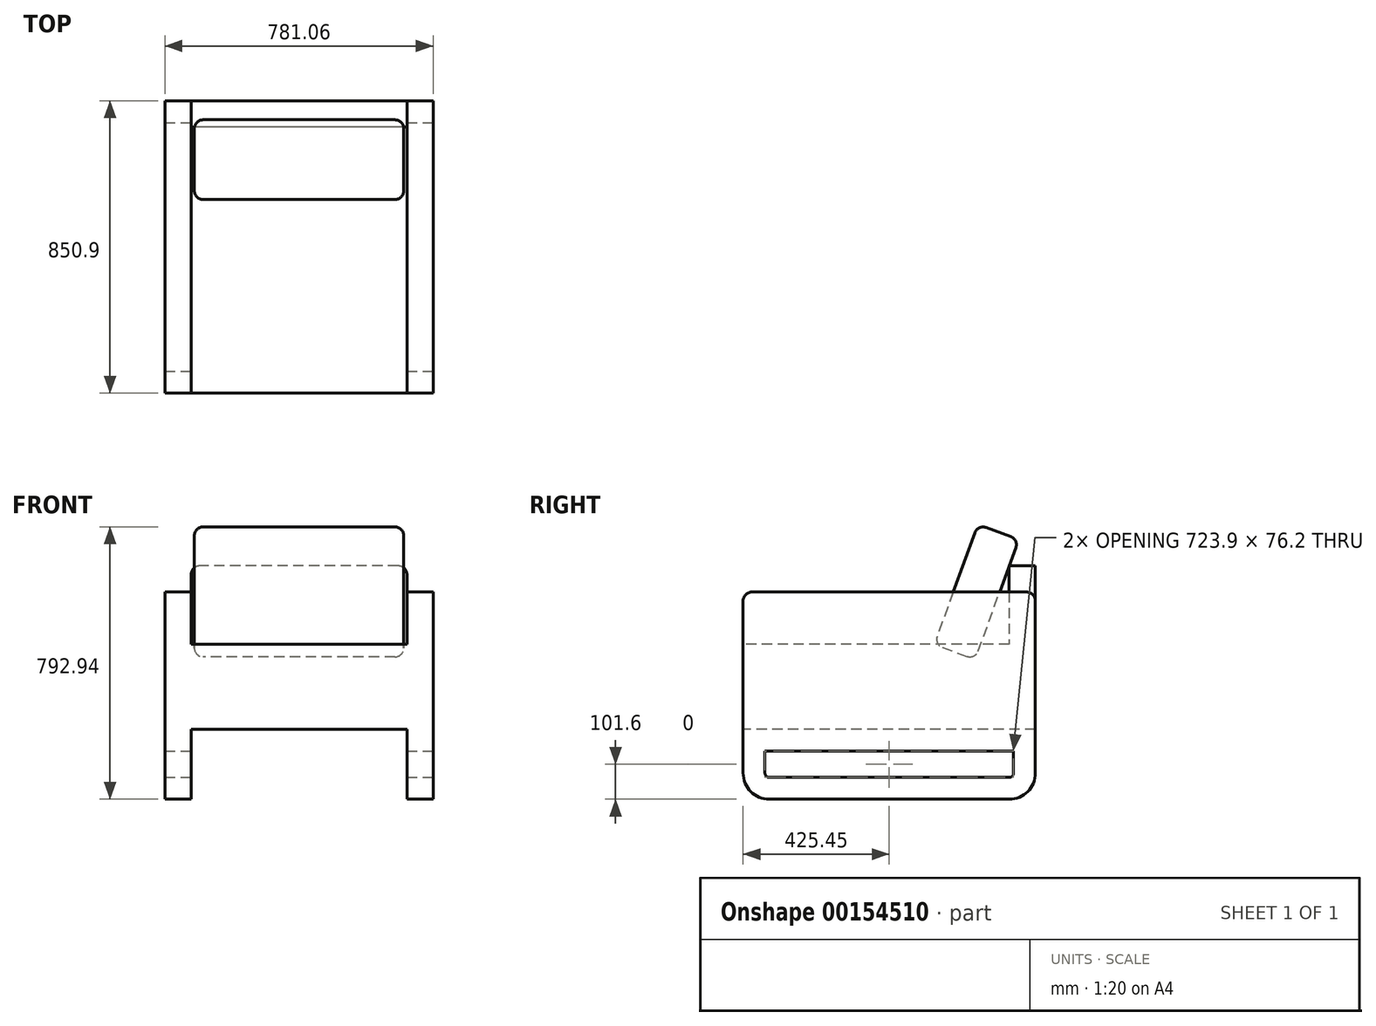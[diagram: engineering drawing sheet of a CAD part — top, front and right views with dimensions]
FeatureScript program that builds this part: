
annotation { "Feature Type Name" : "Feature", "Feature Type Description" : "" }
export const myFeature = defineFeature(function(context is Context, id is Id, definition is map)
    precondition{}
    {
        {
            var Q0;
            Q0=qCreatedBy(makeId("Top.planeOp"),FACE);
            var sketch = newSketch(context, id + "F0", { "sketchPlane" : qUnion([Q0])});
            skLineSegment(sketch, "E0.bottom", {"start": v(390.53, 425.45) * mm, "end": v(-390.52, 425.45) * mm});
            skLineSegment(sketch, "E0.top", {"start": v(390.52, -425.45) * mm, "end": v(-390.53, -425.45) * mm});
            skLineSegment(sketch, "E0.left", {"start": v(390.53, 425.45) * mm, "end": v(390.52, -425.45) * mm});
            skLineSegment(sketch, "E0.right", {"start": v(-390.52, 425.45) * mm, "end": v(-390.53, -425.45) * mm});
            skPoint(sketch, "E0.middle", {"position": v(0, 0) * mm});
            skLineSegment(sketch, "E1", {"start": v(-314.33, -425.45) * mm, "end": v(-314.32, 425.45) * mm});
            skLineSegment(sketch, "E2", {"start": v(314.32, 425.45) * mm, "end": v(314.32, -425.45) * mm});
            skSolve(sketch);
        }
        {
            var Q0;
            {var subQ0=sQuery(id+"F0.wireOp",EDGE,"E1");Q0=makeQuery(id+"F0.imprint","IMPRINT",FACE,{"disambiguationData":[TD([[makeQuery(id+"F0.imprint","IMPRINT",EDGE,{"derivedFrom":subQ0}),-1.0]])]});}
            var Q1;
            {var subQ0=sQuery(id+"F0.wireOp",EDGE,"E0.right");Q1=makeQuery(id+"F0.imprint","IMPRINT",FACE,{"disambiguationData":[TD([[makeQuery(id+"F0.imprint","IMPRINT",EDGE,{"derivedFrom":subQ0}),1.0]])]});}
            var Q2;
            {var subQ0=sQuery(id+"F0.wireOp",EDGE,"E0.left");Q2=makeQuery(id+"F0.imprint","IMPRINT",FACE,{"disambiguationData":[TD([[makeQuery(id+"F0.imprint","IMPRINT",EDGE,{"derivedFrom":subQ0}),-1.0]])]});}
            extrude(context, id + "F1", {"entities" : qUnion([Q0, Q1, Q2]), "depth" : 247.65 * mm});
        }
        {
            var Q0;
            {var subQ0=sQuery(id+"F0.wireOp",EDGE,"E0.right");Q0=makeQuery(id+"F0.imprint","IMPRINT",FACE,{"disambiguationData":[TD([[makeQuery(id+"F0.imprint","IMPRINT",EDGE,{"derivedFrom":subQ0}),1.0]])]});}
            var Q1;
            {var subQ0=sQuery(id+"F0.wireOp",EDGE,"E0.left");Q1=makeQuery(id+"F0.imprint","IMPRINT",FACE,{"disambiguationData":[TD([[makeQuery(id+"F0.imprint","IMPRINT",EDGE,{"derivedFrom":subQ0}),-1.0]])]});}
            extrude(context, id + "F2", {"entities" : qUnion([Q0, Q1]), "operationType" : NewBodyOperationType.ADD, "oppositeDirection" : true, "depth" : 203.2 * mm});
        }
        {
            var Q0;
            Q0=makeQuery(id+"F1.opExtrude","CAP_FACE",FACE,{"disambiguationData":[OSD([sQuery(id+"F0.wireOp",EDGE,"E0.bottom"),sQuery(id+"F0.wireOp",EDGE,"E0.top"),sQuery(id+"F0.wireOp",EDGE,"E0.left"),sQuery(id+"F0.wireOp",EDGE,"E0.right")])],"isStart":false});
            var sketch = newSketch(context, id + "F3", { "sketchPlane" : qUnion([Q0])});
            skLineSegment(sketch, "E3.bottom", {"start": v(390.53, 425.45) * mm, "end": v(314.33, 425.45) * mm});
            skLineSegment(sketch, "E3.top", {"start": v(390.53, -425.45) * mm, "end": v(314.33, -425.45) * mm});
            skLineSegment(sketch, "E3.left", {"start": v(390.53, 425.45) * mm, "end": v(390.53, -425.45) * mm});
            skLineSegment(sketch, "E3.right", {"start": v(314.33, 425.45) * mm, "end": v(314.33, -425.45) * mm});
            skLineSegment(sketch, "E4.bottom", {"start": v(-390.53, -425.45) * mm, "end": v(-314.33, -425.45) * mm});
            skLineSegment(sketch, "E4.top", {"start": v(-390.53, 425.45) * mm, "end": v(-314.33, 425.45) * mm});
            skLineSegment(sketch, "E4.left", {"start": v(-390.53, -425.45) * mm, "end": v(-390.53, 425.45) * mm});
            skLineSegment(sketch, "E4.right", {"start": v(-314.33, -425.45) * mm, "end": v(-314.33, 425.45) * mm});
            skLineSegment(sketch, "E5", {"start": v(-314.33, 425.45) * mm, "end": v(314.33, 425.45) * mm});
            skLineSegment(sketch, "E6", {"start": v(314.33, 349.25) * mm, "end": v(-314.33, 349.25) * mm});
            skSolve(sketch);
        }
        {
            var Q0;
            {var subQ1=sQuery(id+"F3.wireOp",EDGE,"E4.bottom");Q0=makeQuery(id+"F3.imprint","IMPRINT",FACE,{"disambiguationData":[TD([[makeQuery(id+"F3.imprint","IMPRINT",EDGE,{"derivedFrom":subQ1}),-1.0]])]});}
            var Q1;
            {var subQ1=sQuery(id+"F3.wireOp",EDGE,"E3.bottom");Q1=makeQuery(id+"F3.imprint","IMPRINT",FACE,{"disambiguationData":[TD([[makeQuery(id+"F3.imprint","IMPRINT",EDGE,{"derivedFrom":subQ1}),1.0]])]});}
            extrude(context, id + "F4", {"entities" : qUnion([Q0, Q1]), "operationType" : NewBodyOperationType.ADD, "depth" : 152.4 * mm});
        }
        {
            var Q0;
            {var subQ0=sQuery(id+"F3.wireOp",EDGE,"E5");Q0=makeQuery(id+"F3.imprint","IMPRINT",FACE,{"disambiguationData":[TD([[makeQuery(id+"F3.imprint","IMPRINT",EDGE,{"derivedFrom":subQ0}),1.0]])]});}
            extrude(context, id + "F5", {"entities" : qUnion([Q0]), "operationType" : NewBodyOperationType.ADD, "depth" : 228.6 * mm});
        }
        {
            var Q0;
            {var subQ0=sQuery(id+"F0.wireOp",EDGE,"E0.top");Q0=makeQuery(id+"F2.opExtrude","CAP_EDGE",EDGE,{"disambiguationData":[OSD([subQ0]),TDD([makeQuery(id+"F0.imprint","IMPRINT",EDGE,{"disambiguationData":[TD([[makeQuery(id+"F0.imprint","INTERSECT",VERTEX,{"derivedFrom":[subQ0,sQuery(id+"F0.wireOp",EDGE,"E0.right")]}),1.0]])],"derivedFrom":subQ0})])],"isStart":false});}
            var Q1;
            {var subQ0=sQuery(id+"F0.wireOp",EDGE,"E0.top");Q1=makeQuery(id+"F2.opExtrude","CAP_EDGE",EDGE,{"disambiguationData":[OSD([subQ0]),TDD([makeQuery(id+"F0.imprint","IMPRINT",EDGE,{"disambiguationData":[TD([[makeQuery(id+"F0.imprint","INTERSECT",VERTEX,{"derivedFrom":[subQ0,sQuery(id+"F0.wireOp",EDGE,"E0.left")]}),-1.0]])],"derivedFrom":subQ0})])],"isStart":false});}
            var Q2;
            {var subQ0=sQuery(id+"F0.wireOp",EDGE,"E0.bottom");Q2=makeQuery(id+"F2.opExtrude","CAP_EDGE",EDGE,{"disambiguationData":[OSD([subQ0]),TDD([makeQuery(id+"F0.imprint","IMPRINT",EDGE,{"disambiguationData":[TD([[makeQuery(id+"F0.imprint","INTERSECT",VERTEX,{"derivedFrom":[subQ0,sQuery(id+"F0.wireOp",EDGE,"E0.right")]}),1.0]])],"derivedFrom":subQ0})])],"isStart":false});}
            var Q3;
            {var subQ0=sQuery(id+"F0.wireOp",EDGE,"E0.bottom");Q3=makeQuery(id+"F2.opExtrude","CAP_EDGE",EDGE,{"disambiguationData":[OSD([subQ0]),TDD([makeQuery(id+"F0.imprint","IMPRINT",EDGE,{"disambiguationData":[TD([[makeQuery(id+"F0.imprint","INTERSECT",VERTEX,{"derivedFrom":[subQ0,sQuery(id+"F0.wireOp",EDGE,"E0.left")]}),-1.0]])],"derivedFrom":subQ0})])],"isStart":false});}
            fillet(context, id + "F6", {"entities" : qUnion([Q0, Q1, Q2, Q3]), "radius" : 76.2 * mm, "tangentPropagation" : true, "allowEdgeOverflow" : false});
        }
        {
            var Q0;
            Q0=makeQuery(id+"F4.opExtrude","CAP_EDGE",EDGE,{"disambiguationData":[OSD([sQuery(id+"F3.wireOp",EDGE,"E3.bottom")])],"isStart":false});
            var Q1;
            Q1=makeQuery(id+"F4.opExtrude","CAP_EDGE",EDGE,{"disambiguationData":[OSD([sQuery(id+"F3.wireOp",EDGE,"E3.top")])],"isStart":false});
            var Q2;
            Q2=makeQuery(id+"F5.opExtrude","CAP_EDGE",EDGE,{"disambiguationData":[OSD([sQuery(id+"F3.wireOp",EDGE,"E4.right")])],"isStart":false});
            var Q3;
            Q3=makeQuery(id+"F5.opExtrude","CAP_EDGE",EDGE,{"disambiguationData":[OSD([sQuery(id+"F3.wireOp",EDGE,"E3.right")])],"isStart":false});
            var Q4;
            Q4=makeQuery(id+"F4.opExtrude","CAP_EDGE",EDGE,{"disambiguationData":[OSD([sQuery(id+"F3.wireOp",EDGE,"E4.top")])],"isStart":false});
            var Q5;
            Q5=makeQuery(id+"F4.opExtrude","CAP_EDGE",EDGE,{"disambiguationData":[OSD([sQuery(id+"F3.wireOp",EDGE,"E4.bottom")])],"isStart":false});
            fillet(context, id + "F7", {"entities" : qUnion([Q0, Q1, Q2, Q3, Q4, Q5]), "radius" : 25.4 * mm, "tangentPropagation" : true, "allowEdgeOverflow" : false});
        }
        {
            var Q0;
            {var subQ0=sQuery(id+"F0.wireOp",EDGE,"E0.left");Q0=makeQuery(id+"F4.boolean.opBoolean","MERGE",FACE,{"derivedFrom":[makeQuery(id+"F2.boolean.opBoolean","MERGE",FACE,{"derivedFrom":[makeQuery(id+"F1.opExtrude","SWEPT_FACE",FACE,{"disambiguationData":[OSD([subQ0])]}),makeQuery(id+"F2.opExtrude","SWEPT_FACE",FACE,{"disambiguationData":[OSD([subQ0])]})]}),makeQuery(id+"F4.opExtrude","SWEPT_FACE",FACE,{"disambiguationData":[OSD([sQuery(id+"F3.wireOp",EDGE,"E3.left")])]})]});}
            var sketch = newSketch(context, id + "F8", { "sketchPlane" : qUnion([Q0])});
            skLineSegment(sketch, "E7.0", {"start": v(-425.45, 0) * mm, "end": v(425.45, 0) * mm});
            skLineSegment(sketch, "E8.0", {"start": v(-425.45, 0) * mm, "end": v(-425.45, -127) * mm});
            skArc(sketch, "E8.1", {"start": v(-425.45, -127) * mm, "mid": v(-403.13, -180.88) * mm, "end": v(-349.25, -203.2) * mm});
            skLineSegment(sketch, "E8.2", {"start": v(349.25, -203.2) * mm, "end": v(-349.25, -203.2) * mm});
            skLineSegment(sketch, "E8.3", {"start": v(425.45, 0) * mm, "end": v(425.45, -127) * mm});
            skArc(sketch, "E8.4", {"start": v(349.25, -203.2) * mm, "mid": v(403.13, -180.88) * mm, "end": v(425.45, -127) * mm});
            skPoint(sketch, "E9.orphan", {"position": v(-425.45, 374.65) * mm});
            skPoint(sketch, "E10.orphan", {"position": v(425.45, 374.65) * mm});
            skLineSegment(sketch, "E11.0", {"start": v(-361.95, -63.5) * mm, "end": v(-361.95, -127) * mm});
            skLineSegment(sketch, "E11.1", {"start": v(361.95, -63.5) * mm, "end": v(361.95, -127) * mm});
            skArc(sketch, "E11.2", {"start": v(349.25, -139.7) * mm, "mid": v(358.23, -135.98) * mm, "end": v(361.95, -127) * mm});
            skLineSegment(sketch, "E11.3", {"start": v(-361.95, -63.5) * mm, "end": v(361.95, -63.5) * mm});
            skLineSegment(sketch, "E11.4", {"start": v(349.25, -139.7) * mm, "end": v(-349.25, -139.7) * mm});
            skArc(sketch, "E11.5", {"start": v(-361.95, -127) * mm, "mid": v(-358.23, -135.98) * mm, "end": v(-349.25, -139.7) * mm});
            skSolve(sketch);
        }
        {
            var Q0;
            Q0=makeQuery(id+"F8.imprint","IMPRINT",FACE,{"disambiguationData":[TD([[makeQuery(id+"F8.imprint","IMPRINT",EDGE,{"derivedFrom":sQuery(id+"F8.wireOp",EDGE,"E11.0")}),1.0]])]});
            extrude(context, id + "F9", {"entities" : qUnion([Q0]), "operationType" : NewBodyOperationType.REMOVE, "endBound" : BoundingType.THROUGH_ALL, "oppositeDirection" : true, "depth" : 30.48 * mm});
        }
        {
            var Q0;
            Q0=qCreatedBy(makeId("Right.planeOp"),FACE);
            var sketch = newSketch(context, id + "F10", { "sketchPlane" : qUnion([Q0])});
            skLineSegment(sketch, "E12", {"start": v(250.24, 204.21) * mm, "end": v(377.35, 553.46) * mm});
            skLineSegment(sketch, "E13", {"start": v(377.35, 553.46) * mm, "end": v(258.01, 596.9) * mm});
            skLineSegment(sketch, "E14", {"start": v(258.01, 596.9) * mm, "end": v(130.9, 247.65) * mm});
            skLineSegment(sketch, "E15", {"start": v(130.9, 247.65) * mm, "end": v(250.24, 204.21) * mm});
            skLineSegment(sketch, "E16.0", {"start": v(349.25, 450.85) * mm, "end": v(349.25, 476.25) * mm, "construction": true});
            skLineSegment(sketch, "E17.1", {"start": v(-425.45, 247.65) * mm, "end": v(349.25, 247.65) * mm, "construction": true});
            skSolve(sketch);
        }
        {
            var Q0;
            Q0=makeQuery(id+"F10.imprint","IMPRINT",FACE,{"disambiguationData":[TD([[makeQuery(id+"F10.imprint","IMPRINT",EDGE,{"derivedFrom":sQuery(id+"F10.wireOp",EDGE,"E12")}),1.0]])]});
            extrude(context, id + "F11", {"entities" : qUnion([Q0]), "depth" : 609.6 * mm, "symmetric" : true});
        }
        {
            var Q0;
            Q0=makeQuery(id+"F11.opExtrude","SWEPT_FACE",FACE,{"disambiguationData":[OSD([sQuery(id+"F10.wireOp",EDGE,"E14")])]});
            var Q1;
            Q1=makeQuery(id+"F11.opExtrude","SWEPT_FACE",FACE,{"disambiguationData":[OSD([sQuery(id+"F10.wireOp",EDGE,"E13")])]});
            var Q2;
            Q2=makeQuery(id+"F11.opExtrude","CAP_FACE",FACE,{"disambiguationData":[OSD([sQuery(id+"F10.wireOp",EDGE,"E12"),sQuery(id+"F10.wireOp",EDGE,"E13"),sQuery(id+"F10.wireOp",EDGE,"E14"),sQuery(id+"F10.wireOp",EDGE,"E15")])],"isStart":false});
            var Q3;
            Q3=makeQuery(id+"F11.opExtrude","SWEPT_FACE",FACE,{"disambiguationData":[OSD([sQuery(id+"F10.wireOp",EDGE,"E15")])]});
            var Q4;
            Q4=makeQuery(id+"F11.opExtrude","CAP_FACE",FACE,{"disambiguationData":[OSD([sQuery(id+"F10.wireOp",EDGE,"E12"),sQuery(id+"F10.wireOp",EDGE,"E13"),sQuery(id+"F10.wireOp",EDGE,"E14"),sQuery(id+"F10.wireOp",EDGE,"E15")])],"isStart":true});
            var Q5;
            Q5=makeQuery(id+"F11.opExtrude","SWEPT_FACE",FACE,{"disambiguationData":[OSD([sQuery(id+"F10.wireOp",EDGE,"E12")])]});
            fillet(context, id + "F12", {"entities" : qUnion([Q0, Q1, Q2, Q3, Q4, Q5]), "radius" : 25.4 * mm, "tangentPropagation" : true, "allowEdgeOverflow" : false});
        }
    });
